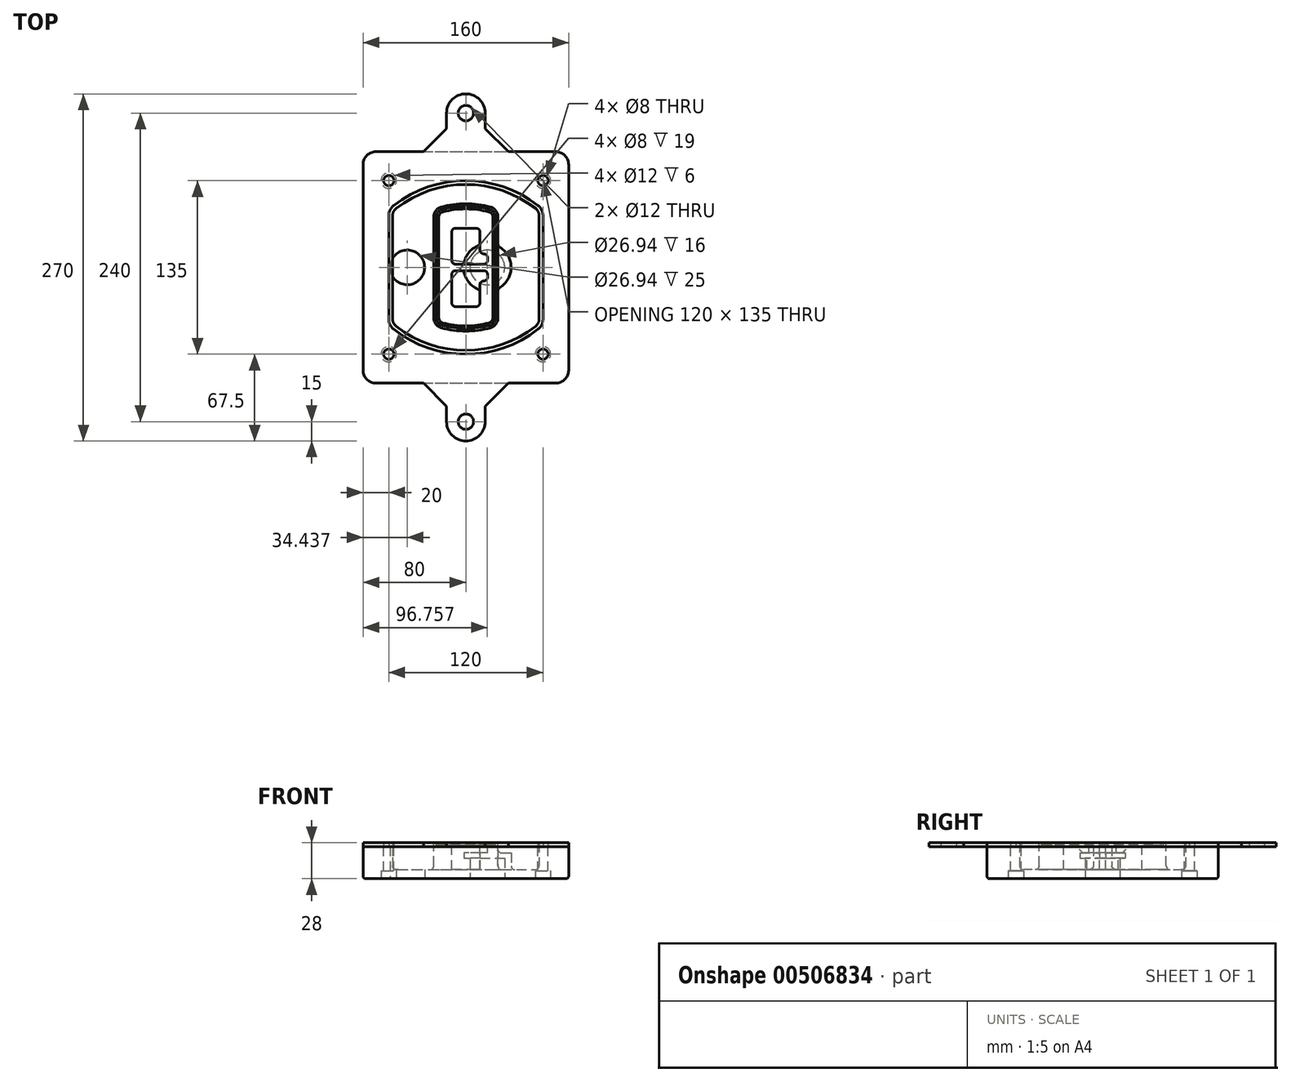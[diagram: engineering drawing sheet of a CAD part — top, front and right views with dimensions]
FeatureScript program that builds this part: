
annotation { "Feature Type Name" : "Feature", "Feature Type Description" : "" }
export const myFeature = defineFeature(function(context is Context, id is Id, definition is map)
    precondition{}
    {
        {
            var Q0;
            Q0=qCreatedBy(makeId("Top.planeOp"),FACE);
            var sketch = newSketch(context, id + "F0", { "sketchPlane" : qUnion([Q0])});
            skPoint(sketch, "E0.rect.middle", {"position": v(0, 0) * mm});
            skLineSegment(sketch, "E1.bottom", {"start": v(-70, -90) * mm, "end": v(70, -90) * mm});
            skLineSegment(sketch, "E1.top", {"start": v(-70, 90) * mm, "end": v(70, 90) * mm});
            skLineSegment(sketch, "E1.left", {"start": v(-80, -80) * mm, "end": v(-80, 80) * mm});
            skLineSegment(sketch, "E1.right", {"start": v(80, -80) * mm, "end": v(80, 80) * mm});
            skLineSegment(sketch, "E2", {"start": v(-80, 90) * mm, "end": v(80, -90) * mm, "construction": true});
            skLineSegment(sketch, "E3", {"start": v(80, 90) * mm, "end": v(-80, -90) * mm, "construction": true});
            skCircle(sketch, "E4", {"center": v(-60, 67.5) * mm, "radius": 4 * mm});
            skCircle(sketch, "E5", {"center": v(60, 67.5) * mm, "radius": 4 * mm});
            skCircle(sketch, "E6", {"center": v(60, -67.5) * mm, "radius": 4 * mm});
            skCircle(sketch, "E7", {"center": v(-60, -67.5) * mm, "radius": 4 * mm});
            skLineSegment(sketch, "E8", {"start": v(-60, 67.5) * mm, "end": v(60, 67.5) * mm, "construction": true});
            skLineSegment(sketch, "E9", {"start": v(60, 67.5) * mm, "end": v(60, -67.5) * mm, "construction": true});
            skLineSegment(sketch, "E10", {"start": v(60, -67.5) * mm, "end": v(-60, -67.5) * mm, "construction": true});
            skLineSegment(sketch, "E11", {"start": v(-60, -67.5) * mm, "end": v(-60, 67.5) * mm, "construction": true});
            skLineSegment(sketch, "E12", {"start": v(-60, 40.3) * mm, "end": v(-60, -40.3) * mm});
            skLineSegment(sketch, "E13", {"start": v(60, 40.3) * mm, "end": v(60, -40.3) * mm});
            skArc(sketch, "E14", {"start": v(56.15, 48.18) * mm, "mid": v(0, 67.5) * mm, "end": v(-56.15, 48.18) * mm});
            skArc(sketch, "E15", {"start": v(-56.15, -48.18) * mm, "mid": v(0, -67.5) * mm, "end": v(56.15, -48.18) * mm});
            skLineSegment(sketch, "E16", {"start": v(-60, 0) * mm, "end": v(60, 0) * mm, "construction": true});
            skPoint(sketch, "E17.visualSharp", {"position": v(-60, -45) * mm});
            skArc(sketch, "E17.filletArc", {"start": v(-60, -40.3) * mm, "mid": v(-58.99, -44.68) * mm, "end": v(-56.15, -48.18) * mm});
            skPoint(sketch, "E18.visualSharp", {"position": v(-60, 45) * mm});
            skArc(sketch, "E18.filletArc", {"start": v(-56.15, 48.18) * mm, "mid": v(-58.99, 44.68) * mm, "end": v(-60, 40.3) * mm});
            skPoint(sketch, "E19.visualSharp", {"position": v(60, 45) * mm});
            skArc(sketch, "E19.filletArc", {"start": v(60, 40.3) * mm, "mid": v(58.99, 44.68) * mm, "end": v(56.15, 48.18) * mm});
            skPoint(sketch, "E20.visualSharp", {"position": v(60, -45) * mm});
            skArc(sketch, "E20.filletArc", {"start": v(56.15, -48.18) * mm, "mid": v(58.99, -44.68) * mm, "end": v(60, -40.3) * mm});
            skPoint(sketch, "E21.visualSharp", {"position": v(-80, 90) * mm});
            skArc(sketch, "E21.filletArc", {"start": v(-70, 90) * mm, "mid": v(-77.07, 87.07) * mm, "end": v(-80, 80) * mm});
            skPoint(sketch, "E22.visualSharp", {"position": v(80, 90) * mm});
            skArc(sketch, "E22.filletArc", {"start": v(80, 80) * mm, "mid": v(77.07, 87.07) * mm, "end": v(70, 90) * mm});
            skPoint(sketch, "E23.visualSharp", {"position": v(80, -90) * mm});
            skArc(sketch, "E23.filletArc", {"start": v(70, -90) * mm, "mid": v(77.07, -87.07) * mm, "end": v(80, -80) * mm});
            skPoint(sketch, "E24.visualSharp", {"position": v(-80, -90) * mm});
            skArc(sketch, "E24.filletArc", {"start": v(-80, -80) * mm, "mid": v(-77.07, -87.07) * mm, "end": v(-70, -90) * mm});
            skArc(sketch, "E25.0", {"start": v(57, 40.3) * mm, "mid": v(56.3, 43.36) * mm, "end": v(54.3, 45.81) * mm});
            skLineSegment(sketch, "E25.1", {"start": v(57, 40.3) * mm, "end": v(57, -40.3) * mm});
            skArc(sketch, "E25.2", {"start": v(54.3, -45.81) * mm, "mid": v(56.3, -43.36) * mm, "end": v(57, -40.3) * mm});
            skArc(sketch, "E25.3", {"start": v(-54.3, -45.81) * mm, "mid": v(0, -64.5) * mm, "end": v(54.3, -45.81) * mm});
            skArc(sketch, "E25.4", {"start": v(-57, -40.3) * mm, "mid": v(-56.3, -43.36) * mm, "end": v(-54.3, -45.81) * mm});
            skArc(sketch, "E25.5", {"start": v(54.3, 45.81) * mm, "mid": v(0, 64.5) * mm, "end": v(-54.3, 45.81) * mm});
            skLineSegment(sketch, "E25.6", {"start": v(-57, 40.3) * mm, "end": v(-57, -40.3) * mm});
            skArc(sketch, "E25.7", {"start": v(-54.3, 45.81) * mm, "mid": v(-56.3, 43.36) * mm, "end": v(-57, 40.3) * mm});
            skArc(sketch, "E26.0", {"start": v(-58.62, 51.33) * mm, "mid": v(-62.58, 46.43) * mm, "end": v(-64, 40.3) * mm});
            skArc(sketch, "E26.1", {"start": v(58.62, 51.33) * mm, "mid": v(0, 71.5) * mm, "end": v(-58.62, 51.33) * mm});
            skArc(sketch, "E26.2", {"start": v(64, 40.3) * mm, "mid": v(62.58, 46.43) * mm, "end": v(58.62, 51.33) * mm});
            skLineSegment(sketch, "E26.3", {"start": v(64, 40.3) * mm, "end": v(64, -40.3) * mm});
            skArc(sketch, "E26.4", {"start": v(58.62, -51.33) * mm, "mid": v(62.58, -46.43) * mm, "end": v(64, -40.3) * mm});
            skLineSegment(sketch, "E26.5", {"start": v(-64, 40.3) * mm, "end": v(-64, -40.3) * mm});
            skArc(sketch, "E26.6", {"start": v(-58.62, -51.33) * mm, "mid": v(0, -71.5) * mm, "end": v(58.62, -51.33) * mm});
            skArc(sketch, "E26.7", {"start": v(-64, -40.3) * mm, "mid": v(-62.58, -46.43) * mm, "end": v(-58.62, -51.33) * mm});
            skSolve(sketch);
        }
        {
            var Q0;
            Q0=makeQuery(id+"F0.imprint","IMPRINT",FACE,{"disambiguationData":[TD([[makeQuery(id+"F0.imprint","IMPRINT",EDGE,{"derivedFrom":sQuery(id+"F0.wireOp",EDGE,"E1.bottom")}),1.0]])]});
            var Q1;
            Q1=makeQuery(id+"F0.imprint","IMPRINT",FACE,{"disambiguationData":[TD([[makeQuery(id+"F0.imprint","IMPRINT",EDGE,{"derivedFrom":sQuery(id+"F0.wireOp",EDGE,"E12")}),1.0]])]});
            var Q2;
            Q2=makeQuery(id+"F0.imprint","IMPRINT",FACE,{"disambiguationData":[TD([[makeQuery(id+"F0.imprint","IMPRINT",EDGE,{"derivedFrom":sQuery(id+"F0.wireOp",EDGE,"E25.0")}),1.0]])]});
            var Q3;
            Q3=makeQuery(id+"F0.imprint","IMPRINT",FACE,{"disambiguationData":[TD([[makeQuery(id+"F0.imprint","IMPRINT",EDGE,{"derivedFrom":sQuery(id+"F0.wireOp",EDGE,"E12")}),-1.0]])]});
            extrude(context, id + "F1", {"entities" : qUnion([Q0, Q1, Q2, Q3]), "oppositeDirection" : true, "depth" : 25 * mm});
        }
        {
            var Q0;
            Q0=makeQuery(id+"F0.imprint","IMPRINT",FACE,{"disambiguationData":[TD([[makeQuery(id+"F0.imprint","IMPRINT",EDGE,{"derivedFrom":sQuery(id+"F0.wireOp",EDGE,"E12")}),1.0]])]});
            extrude(context, id + "F2", {"entities" : qUnion([Q0]), "operationType" : NewBodyOperationType.ADD, "depth" : 3 * mm});
        }
        {
            var Q0;
            Q0=makeQuery(id+"F0.imprint","IMPRINT",FACE,{"disambiguationData":[TD([[makeQuery(id+"F0.imprint","IMPRINT",EDGE,{"derivedFrom":sQuery(id+"F0.wireOp",EDGE,"E25.0")}),1.0]])]});
            extrude(context, id + "F3", {"entities" : qUnion([Q0]), "operationType" : NewBodyOperationType.REMOVE, "oppositeDirection" : true, "depth" : 18 * mm});
        }
        {
            var Q0;
            Q0=makeQuery(id+"F2.opExtrude","CAP_FACE",FACE,{"disambiguationData":[OSD([sQuery(id+"F0.wireOp",EDGE,"E12"),sQuery(id+"F0.wireOp",EDGE,"E13"),sQuery(id+"F0.wireOp",EDGE,"E14"),sQuery(id+"F0.wireOp",EDGE,"E15"),sQuery(id+"F0.wireOp",EDGE,"E17.filletArc"),sQuery(id+"F0.wireOp",EDGE,"E18.filletArc"),sQuery(id+"F0.wireOp",EDGE,"E19.filletArc"),sQuery(id+"F0.wireOp",EDGE,"E20.filletArc"),sQuery(id+"F0.wireOp",EDGE,"E25.0"),sQuery(id+"F0.wireOp",EDGE,"E25.1"),sQuery(id+"F0.wireOp",EDGE,"E25.2"),sQuery(id+"F0.wireOp",EDGE,"E25.3"),sQuery(id+"F0.wireOp",EDGE,"E25.4"),sQuery(id+"F0.wireOp",EDGE,"E25.5"),sQuery(id+"F0.wireOp",EDGE,"E25.6"),sQuery(id+"F0.wireOp",EDGE,"E25.7")])],"isStart":false});
            var sketch = newSketch(context, id + "F4", { "sketchPlane" : qUnion([Q0])});
            skArc(sketch, "E27.0", {"start": v(-19.08, -46.97) * mm, "mid": v(0, -49.5) * mm, "end": v(19.08, -46.97) * mm});
            skArc(sketch, "E28.0", {"start": v(19.08, 46.97) * mm, "mid": v(0, 49.5) * mm, "end": v(-19.08, 46.97) * mm});
            skLineSegment(sketch, "E29", {"start": v(-25, 39.25) * mm, "end": v(-25, -39.25) * mm});
            skLineSegment(sketch, "E30", {"start": v(25, 39.25) * mm, "end": v(25, -39.25) * mm});
            skLineSegment(sketch, "E31", {"start": v(-25, 45.1) * mm, "end": v(25, 45.1) * mm, "construction": true});
            skLineSegment(sketch, "E32", {"start": v(-25, -45.1) * mm, "end": v(25, -45.1) * mm, "construction": true});
            skPoint(sketch, "E33.visualSharp", {"position": v(-25, 45.1) * mm});
            skArc(sketch, "E33.filletArc", {"start": v(-19.08, 46.97) * mm, "mid": v(-23.35, 44.11) * mm, "end": v(-25, 39.25) * mm});
            skPoint(sketch, "E34.visualSharp", {"position": v(25, 45.1) * mm});
            skArc(sketch, "E34.filletArc", {"start": v(25, 39.25) * mm, "mid": v(23.35, 44.11) * mm, "end": v(19.08, 46.97) * mm});
            skPoint(sketch, "E35.visualSharp", {"position": v(25, -45.1) * mm});
            skArc(sketch, "E35.filletArc", {"start": v(19.08, -46.97) * mm, "mid": v(23.35, -44.11) * mm, "end": v(25, -39.25) * mm});
            skPoint(sketch, "E36.visualSharp", {"position": v(-25, -45.1) * mm});
            skArc(sketch, "E36.filletArc", {"start": v(-25, -39.25) * mm, "mid": v(-23.35, -44.11) * mm, "end": v(-19.08, -46.97) * mm});
            skArc(sketch, "E37.0", {"start": v(54.3, 45.81) * mm, "mid": v(0, 64.5) * mm, "end": v(-54.3, 45.81) * mm});
            skArc(sketch, "E37.1", {"start": v(-54.3, 45.81) * mm, "mid": v(-56.3, 43.36) * mm, "end": v(-57, 40.3) * mm});
            skLineSegment(sketch, "E37.2", {"start": v(-57, 40.3) * mm, "end": v(-57, -40.3) * mm});
            skArc(sketch, "E37.3", {"start": v(-57, -40.3) * mm, "mid": v(-56.3, -43.36) * mm, "end": v(-54.3, -45.81) * mm});
            skArc(sketch, "E37.4", {"start": v(-54.3, -45.81) * mm, "mid": v(0, -64.5) * mm, "end": v(54.3, -45.81) * mm});
            skArc(sketch, "E37.5", {"start": v(54.3, -45.81) * mm, "mid": v(56.3, -43.36) * mm, "end": v(57, -40.3) * mm});
            skLineSegment(sketch, "E37.6", {"start": v(57, 40.3) * mm, "end": v(57, -40.3) * mm});
            skArc(sketch, "E37.7", {"start": v(57, 40.3) * mm, "mid": v(56.3, 43.36) * mm, "end": v(54.3, 45.81) * mm});
            skLineSegment(sketch, "E38.0", {"start": v(23, 39.25) * mm, "end": v(23, -39.25) * mm});
            skArc(sketch, "E38.1", {"start": v(18.56, -45.04) * mm, "mid": v(21.76, -42.9) * mm, "end": v(23, -39.25) * mm});
            skArc(sketch, "E38.2", {"start": v(-18.56, -45.04) * mm, "mid": v(0, -47.5) * mm, "end": v(18.56, -45.04) * mm});
            skArc(sketch, "E38.3", {"start": v(-23, -39.25) * mm, "mid": v(-21.76, -42.9) * mm, "end": v(-18.56, -45.04) * mm});
            skLineSegment(sketch, "E38.4", {"start": v(-23, 39.25) * mm, "end": v(-23, -39.25) * mm});
            skArc(sketch, "E38.5", {"start": v(23, 39.25) * mm, "mid": v(21.76, 42.9) * mm, "end": v(18.56, 45.04) * mm});
            skArc(sketch, "E38.6", {"start": v(-18.56, 45.04) * mm, "mid": v(-21.76, 42.9) * mm, "end": v(-23, 39.25) * mm});
            skArc(sketch, "E38.7", {"start": v(18.56, 45.04) * mm, "mid": v(0, 47.5) * mm, "end": v(-18.56, 45.04) * mm});
            skArc(sketch, "E39.0", {"start": v(21, 39.25) * mm, "mid": v(20.18, 41.68) * mm, "end": v(18.04, 43.1) * mm});
            skLineSegment(sketch, "E39.1", {"start": v(21, 39.25) * mm, "end": v(21, -39.25) * mm});
            skArc(sketch, "E39.2", {"start": v(18.04, -43.1) * mm, "mid": v(20.18, -41.68) * mm, "end": v(21, -39.25) * mm});
            skArc(sketch, "E39.3", {"start": v(-18.04, -43.1) * mm, "mid": v(0, -45.5) * mm, "end": v(18.04, -43.1) * mm});
            skArc(sketch, "E39.4", {"start": v(-21, -39.25) * mm, "mid": v(-20.18, -41.68) * mm, "end": v(-18.04, -43.1) * mm});
            skArc(sketch, "E39.5", {"start": v(18.04, 43.1) * mm, "mid": v(0, 45.5) * mm, "end": v(-18.04, 43.1) * mm});
            skLineSegment(sketch, "E39.6", {"start": v(-21, 39.25) * mm, "end": v(-21, -39.25) * mm});
            skArc(sketch, "E39.7", {"start": v(-18.04, 43.1) * mm, "mid": v(-20.18, 41.68) * mm, "end": v(-21, 39.25) * mm});
            skLineSegment(sketch, "E40", {"start": v(-25, 0) * mm, "end": v(25, 0) * mm, "construction": true});
            skLineSegment(sketch, "E41", {"start": v(-11, 5.5) * mm, "end": v(-11, 27.5) * mm});
            skLineSegment(sketch, "E42", {"start": v(-8, 30.5) * mm, "end": v(8, 30.5) * mm});
            skLineSegment(sketch, "E43", {"start": v(11, 27.5) * mm, "end": v(11, 13.5) * mm});
            skLineSegment(sketch, "E44", {"start": v(14, 10.5) * mm, "end": v(14, 10.5) * mm});
            skLineSegment(sketch, "E45", {"start": v(17, 7.5) * mm, "end": v(17, 5.5) * mm});
            skLineSegment(sketch, "E46", {"start": v(14, 2.5) * mm, "end": v(-8, 2.5) * mm});
            skPoint(sketch, "E47.visualSharp", {"position": v(-11, 30.5) * mm});
            skArc(sketch, "E47.filletArc", {"start": v(-8, 30.5) * mm, "mid": v(-10.12, 29.62) * mm, "end": v(-11, 27.5) * mm});
            skPoint(sketch, "E48.visualSharp", {"position": v(11, 30.5) * mm});
            skArc(sketch, "E48.filletArc", {"start": v(11, 27.5) * mm, "mid": v(10.12, 29.62) * mm, "end": v(8, 30.5) * mm});
            skPoint(sketch, "E49.visualSharp", {"position": v(11, 10.5) * mm});
            skArc(sketch, "E49.filletArc", {"start": v(11, 13.5) * mm, "mid": v(11.88, 11.38) * mm, "end": v(14, 10.5) * mm});
            skPoint(sketch, "E50.visualSharp", {"position": v(17, 10.5) * mm});
            skArc(sketch, "E50.filletArc", {"start": v(17, 7.5) * mm, "mid": v(16.12, 9.62) * mm, "end": v(14, 10.5) * mm});
            skPoint(sketch, "E51.visualSharp", {"position": v(17, 2.5) * mm});
            skArc(sketch, "E51.filletArc", {"start": v(14, 2.5) * mm, "mid": v(16.12, 3.38) * mm, "end": v(17, 5.5) * mm});
            skPoint(sketch, "E52.visualSharp", {"position": v(-11, 2.5) * mm});
            skArc(sketch, "E52.filletArc", {"start": v(-11, 5.5) * mm, "mid": v(-10.12, 3.38) * mm, "end": v(-8, 2.5) * mm});
            skLineSegment(sketch, "E53.0.MirrorCS", {"start": v(14, -2.5) * mm, "end": v(-8, -2.5) * mm});
            skArc(sketch, "E54.0.MirrorCS", {"start": v(-11, -5.5) * mm, "mid": v(-10.12, -3.38) * mm, "end": v(-8, -2.5) * mm});
            skLineSegment(sketch, "E55.0.MirrorCS", {"start": v(-11, -5.5) * mm, "end": v(-11, -27.5) * mm});
            skArc(sketch, "E56.0.MirrorCS", {"start": v(-8, -30.5) * mm, "mid": v(-10.12, -29.62) * mm, "end": v(-11, -27.5) * mm});
            skLineSegment(sketch, "E57.0.MirrorCS", {"start": v(-8, -30.5) * mm, "end": v(8, -30.5) * mm});
            skArc(sketch, "E58.0.MirrorCS", {"start": v(11, -27.5) * mm, "mid": v(10.12, -29.62) * mm, "end": v(8, -30.5) * mm});
            skLineSegment(sketch, "E59.0.MirrorCS", {"start": v(11, -27.5) * mm, "end": v(11, -13.5) * mm});
            skArc(sketch, "E60.0.MirrorCS", {"start": v(11, -13.5) * mm, "mid": v(11.88, -11.38) * mm, "end": v(14, -10.5) * mm});
            skArc(sketch, "E61.0.MirrorCS", {"start": v(17, -7.5) * mm, "mid": v(16.12, -9.62) * mm, "end": v(14, -10.5) * mm});
            skLineSegment(sketch, "E62.0.MirrorCS", {"start": v(17, -7.5) * mm, "end": v(17, -5.5) * mm});
            skArc(sketch, "E63.0.MirrorCS", {"start": v(14, -2.5) * mm, "mid": v(16.12, -3.38) * mm, "end": v(17, -5.5) * mm});
            skSolve(sketch);
        }
        {
            var Q0;
            Q0=makeQuery(id+"F4.imprint","IMPRINT",FACE,{"disambiguationData":[TD([[makeQuery(id+"F4.imprint","IMPRINT",EDGE,{"derivedFrom":sQuery(id+"F4.wireOp",EDGE,"E27.0")}),1.0]])]});
            var Q1;
            Q1=makeQuery(id+"F4.imprint","IMPRINT",FACE,{"disambiguationData":[TD([[makeQuery(id+"F4.imprint","IMPRINT",EDGE,{"derivedFrom":sQuery(id+"F4.wireOp",EDGE,"E38.0")}),-1.0]])]});
            var Q2;
            Q2=makeQuery(id+"F4.imprint","IMPRINT",FACE,{"disambiguationData":[TD([[makeQuery(id+"F4.imprint","IMPRINT",EDGE,{"derivedFrom":sQuery(id+"F4.wireOp",EDGE,"E39.0")}),1.0]])]});
            extrude(context, id + "F5", {"entities" : qUnion([Q0, Q1, Q2]), "operationType" : NewBodyOperationType.ADD, "endBound" : BoundingType.UP_TO_NEXT, "oppositeDirection" : true, "depth" : 25 * mm});
        }
        {
            var Q0;
            Q0=makeQuery(id+"F4.imprint","IMPRINT",FACE,{"disambiguationData":[TD([[makeQuery(id+"F4.imprint","IMPRINT",EDGE,{"derivedFrom":sQuery(id+"F4.wireOp",EDGE,"E38.0")}),-1.0]])]});
            extrude(context, id + "F6", {"entities" : qUnion([Q0]), "operationType" : NewBodyOperationType.REMOVE, "oppositeDirection" : true, "depth" : 2 * mm});
        }
        {
            var Q0;
            Q0=makeQuery(id+"F1.opExtrude","CAP_FACE",FACE,{"disambiguationData":[OSD([sQuery(id+"F0.wireOp",EDGE,"E1.bottom"),sQuery(id+"F0.wireOp",EDGE,"E1.top"),sQuery(id+"F0.wireOp",EDGE,"E1.left"),sQuery(id+"F0.wireOp",EDGE,"E1.right"),sQuery(id+"F0.wireOp",EDGE,"E4"),sQuery(id+"F0.wireOp",EDGE,"E5"),sQuery(id+"F0.wireOp",EDGE,"E6"),sQuery(id+"F0.wireOp",EDGE,"E7"),sQuery(id+"F0.wireOp",EDGE,"E21.filletArc"),sQuery(id+"F0.wireOp",EDGE,"E22.filletArc"),sQuery(id+"F0.wireOp",EDGE,"E23.filletArc"),sQuery(id+"F0.wireOp",EDGE,"E24.filletArc")])],"isStart":false});
            var sketch = newSketch(context, id + "F7", { "sketchPlane" : qUnion([Q0])});
            skCircle(sketch, "E64", {"center": v(16.76, 0) * mm, "radius": 13.47 * mm});
            skCircle(sketch, "E65", {"center": v(-45.56, 0) * mm, "radius": 13.47 * mm});
            skLineSegment(sketch, "E66", {"start": v(80, 0) * mm, "end": v(-80, 0) * mm});
            skCircle(sketch, "E67", {"center": v(16.76, 0) * mm, "radius": 18.47 * mm});
            skCircle(sketch, "E68", {"center": v(60, -67.5) * mm, "radius": 6 * mm});
            skCircle(sketch, "E69", {"center": v(-60, -67.5) * mm, "radius": 6 * mm});
            skCircle(sketch, "E70", {"center": v(-60, 67.5) * mm, "radius": 6 * mm});
            skCircle(sketch, "E71", {"center": v(60, 67.5) * mm, "radius": 6 * mm});
            skSolve(sketch);
        }
        {
            var Q0;
            {var subQ1=sQuery(id+"F7.wireOp",EDGE,"E66");var subQ4=sQuery(id+"F7.wireOp",EDGE,"E64");var subQ6=makeQuery(id+"F7.imprint","INTERSECT",VERTEX,{"disambiguationData":[OD(0.0)],"derivedFrom":[subQ4,subQ1]});Q0=makeQuery(id+"F7.imprint","IMPRINT",FACE,{"disambiguationData":[TD([[makeQuery(id+"F7.imprint","IMPRINT",EDGE,{"disambiguationData":[TD([[subQ6,-1.0]])],"derivedFrom":subQ4}),-1.0]])]});}
            var Q1;
            {var subQ0=sQuery(id+"F7.wireOp",EDGE,"E66");var subQ1=sQuery(id+"F7.wireOp",EDGE,"E64");var subQ3=makeQuery(id+"F7.imprint","INTERSECT",VERTEX,{"disambiguationData":[OD(0.0)],"derivedFrom":[subQ1,subQ0]});Q1=makeQuery(id+"F7.imprint","IMPRINT",FACE,{"disambiguationData":[TD([[makeQuery(id+"F7.imprint","IMPRINT",EDGE,{"disambiguationData":[TD([[subQ3,-1.0]])],"derivedFrom":subQ1}),1.0]])]});}
            var Q2;
            {var subQ0=sQuery(id+"F7.wireOp",EDGE,"E66");var subQ1=sQuery(id+"F7.wireOp",EDGE,"E64");var subQ3=makeQuery(id+"F7.imprint","INTERSECT",VERTEX,{"disambiguationData":[OD(0.0)],"derivedFrom":[subQ1,subQ0]});Q2=makeQuery(id+"F7.imprint","IMPRINT",FACE,{"disambiguationData":[TD([[makeQuery(id+"F7.imprint","IMPRINT",EDGE,{"disambiguationData":[TD([[subQ3,1.0]])],"derivedFrom":subQ1}),1.0]])]});}
            var Q3;
            {var subQ1=sQuery(id+"F7.wireOp",EDGE,"E66");var subQ4=sQuery(id+"F7.wireOp",EDGE,"E64");var subQ6=makeQuery(id+"F7.imprint","INTERSECT",VERTEX,{"disambiguationData":[OD(0.0)],"derivedFrom":[subQ4,subQ1]});Q3=makeQuery(id+"F7.imprint","IMPRINT",FACE,{"disambiguationData":[TD([[makeQuery(id+"F7.imprint","IMPRINT",EDGE,{"disambiguationData":[TD([[subQ6,1.0]])],"derivedFrom":subQ4}),-1.0]])]});}
            extrude(context, id + "F8", {"entities" : qUnion([Q0, Q1, Q2, Q3]), "operationType" : NewBodyOperationType.ADD, "oppositeDirection" : true, "depth" : 20 * mm});
        }
        {
            var Q0;
            {var subQ0=sQuery(id+"F7.wireOp",EDGE,"E66");var subQ1=sQuery(id+"F7.wireOp",EDGE,"E64");var subQ3=makeQuery(id+"F7.imprint","INTERSECT",VERTEX,{"disambiguationData":[OD(0.0)],"derivedFrom":[subQ1,subQ0]});Q0=makeQuery(id+"F7.imprint","IMPRINT",FACE,{"disambiguationData":[TD([[makeQuery(id+"F7.imprint","IMPRINT",EDGE,{"disambiguationData":[TD([[subQ3,-1.0]])],"derivedFrom":subQ1}),1.0]])]});}
            var Q1;
            {var subQ0=sQuery(id+"F7.wireOp",EDGE,"E66");var subQ1=sQuery(id+"F7.wireOp",EDGE,"E64");var subQ3=makeQuery(id+"F7.imprint","INTERSECT",VERTEX,{"disambiguationData":[OD(0.0)],"derivedFrom":[subQ1,subQ0]});Q1=makeQuery(id+"F7.imprint","IMPRINT",FACE,{"disambiguationData":[TD([[makeQuery(id+"F7.imprint","IMPRINT",EDGE,{"disambiguationData":[TD([[subQ3,1.0]])],"derivedFrom":subQ1}),1.0]])]});}
            extrude(context, id + "F9", {"entities" : qUnion([Q0, Q1]), "operationType" : NewBodyOperationType.REMOVE, "oppositeDirection" : true, "depth" : 16 * mm});
        }
        {
            var Q0;
            {var subQ0=sQuery(id+"F7.wireOp",EDGE,"E66");var subQ1=sQuery(id+"F7.wireOp",EDGE,"E65");var subQ3=makeQuery(id+"F7.imprint","INTERSECT",VERTEX,{"disambiguationData":[OD(0.0)],"derivedFrom":[subQ1,subQ0]});Q0=makeQuery(id+"F7.imprint","IMPRINT",FACE,{"disambiguationData":[TD([[makeQuery(id+"F7.imprint","IMPRINT",EDGE,{"disambiguationData":[TD([[subQ3,-1.0]])],"derivedFrom":subQ1}),1.0]])]});}
            var Q1;
            {var subQ0=sQuery(id+"F7.wireOp",EDGE,"E66");var subQ1=sQuery(id+"F7.wireOp",EDGE,"E65");var subQ3=makeQuery(id+"F7.imprint","INTERSECT",VERTEX,{"disambiguationData":[OD(0.0)],"derivedFrom":[subQ1,subQ0]});Q1=makeQuery(id+"F7.imprint","IMPRINT",FACE,{"disambiguationData":[TD([[makeQuery(id+"F7.imprint","IMPRINT",EDGE,{"disambiguationData":[TD([[subQ3,1.0]])],"derivedFrom":subQ1}),1.0]])]});}
            extrude(context, id + "F10", {"entities" : qUnion([Q0, Q1]), "operationType" : NewBodyOperationType.REMOVE, "oppositeDirection" : true, "depth" : 25 * mm});
        }
        {
            var Q0;
            Q0=makeQuery(id+"F7.imprint","IMPRINT",FACE,{"disambiguationData":[TD([[makeQuery(id+"F7.imprint","IMPRINT",EDGE,{"derivedFrom":sQuery(id+"F7.wireOp",EDGE,"E68")}),1.0]])]});
            var Q1;
            Q1=makeQuery(id+"F7.imprint","IMPRINT",FACE,{"disambiguationData":[TD([[makeQuery(id+"F7.imprint","IMPRINT",EDGE,{"derivedFrom":makeQuery(id+"F1.opExtrude","CAP_EDGE",EDGE,{"disambiguationData":[OSD([sQuery(id+"F0.wireOp",EDGE,"E5")])],"isStart":false})}),-1.0]])]});
            var Q2;
            Q2=makeQuery(id+"F7.imprint","IMPRINT",FACE,{"disambiguationData":[TD([[makeQuery(id+"F7.imprint","IMPRINT",EDGE,{"derivedFrom":sQuery(id+"F7.wireOp",EDGE,"E69")}),1.0]])]});
            var Q3;
            Q3=makeQuery(id+"F7.imprint","IMPRINT",FACE,{"disambiguationData":[TD([[makeQuery(id+"F7.imprint","IMPRINT",EDGE,{"derivedFrom":makeQuery(id+"F1.opExtrude","CAP_EDGE",EDGE,{"disambiguationData":[OSD([sQuery(id+"F0.wireOp",EDGE,"E4")])],"isStart":false})}),-1.0]])]});
            var Q4;
            Q4=makeQuery(id+"F7.imprint","IMPRINT",FACE,{"disambiguationData":[TD([[makeQuery(id+"F7.imprint","IMPRINT",EDGE,{"derivedFrom":sQuery(id+"F7.wireOp",EDGE,"E70")}),1.0]])]});
            var Q5;
            Q5=makeQuery(id+"F7.imprint","IMPRINT",FACE,{"disambiguationData":[TD([[makeQuery(id+"F7.imprint","IMPRINT",EDGE,{"derivedFrom":makeQuery(id+"F1.opExtrude","CAP_EDGE",EDGE,{"disambiguationData":[OSD([sQuery(id+"F0.wireOp",EDGE,"E7")])],"isStart":false})}),-1.0]])]});
            var Q6;
            Q6=makeQuery(id+"F7.imprint","IMPRINT",FACE,{"disambiguationData":[TD([[makeQuery(id+"F7.imprint","IMPRINT",EDGE,{"derivedFrom":sQuery(id+"F7.wireOp",EDGE,"E71")}),1.0]])]});
            var Q7;
            Q7=makeQuery(id+"F7.imprint","IMPRINT",FACE,{"disambiguationData":[TD([[makeQuery(id+"F7.imprint","IMPRINT",EDGE,{"derivedFrom":makeQuery(id+"F1.opExtrude","CAP_EDGE",EDGE,{"disambiguationData":[OSD([sQuery(id+"F0.wireOp",EDGE,"E6")])],"isStart":false})}),-1.0]])]});
            extrude(context, id + "F11", {"entities" : qUnion([Q0, Q1, Q2, Q3, Q4, Q5, Q6, Q7]), "operationType" : NewBodyOperationType.REMOVE, "oppositeDirection" : true, "depth" : 6 * mm});
        }
        {
            var Q0;
            Q0=makeQuery(id+"F9.boolean.opBoolean","COPY",FACE,{"derivedFrom":makeQuery(id+"F9.opExtrude","CAP_FACE",FACE,{"disambiguationData":[OSD([sQuery(id+"F7.wireOp",EDGE,"E64")])],"isStart":false})});
            var sketch = newSketch(context, id + "F12", { "sketchPlane" : qUnion([Q0])});
            skArc(sketch, "E72.0", {"start": v(11, 17.55) * mm, "mid": v(2.57, 11.82) * mm, "end": v(-1.54, 2.5) * mm});
            skArc(sketch, "E72.1", {"start": v(-1.54, -2.5) * mm, "mid": v(2.57, -11.82) * mm, "end": v(11, -17.55) * mm});
            skLineSegment(sketch, "E73", {"start": v(-1.54, -2.5) * mm, "end": v(14, -2.5) * mm});
            skLineSegment(sketch, "E74.0", {"start": v(14, 2.5) * mm, "end": v(-1.54, 2.5) * mm});
            skArc(sketch, "E74.1", {"start": v(14, 2.5) * mm, "mid": v(16.12, 3.38) * mm, "end": v(17, 5.5) * mm});
            skLineSegment(sketch, "E74.2", {"start": v(17, 7.5) * mm, "end": v(17, 5.5) * mm});
            skArc(sketch, "E74.3", {"start": v(17, 7.5) * mm, "mid": v(16.12, 9.62) * mm, "end": v(14, 10.5) * mm});
            skArc(sketch, "E74.4", {"start": v(11, 13.5) * mm, "mid": v(11.88, 11.38) * mm, "end": v(14, 10.5) * mm});
            skLineSegment(sketch, "E74.5", {"start": v(11, 17.55) * mm, "end": v(11, 13.5) * mm});
            skLineSegment(sketch, "E74.7", {"start": v(14, -2.5) * mm, "end": v(-1.54, -2.5) * mm});
            skArc(sketch, "E74.8", {"start": v(14, -2.5) * mm, "mid": v(16.12, -3.38) * mm, "end": v(17, -5.5) * mm});
            skLineSegment(sketch, "E74.9", {"start": v(17, -7.5) * mm, "end": v(17, -5.5) * mm});
            skArc(sketch, "E74.10", {"start": v(17, -7.5) * mm, "mid": v(16.12, -9.62) * mm, "end": v(14, -10.5) * mm});
            skArc(sketch, "E74.11", {"start": v(11, -13.5) * mm, "mid": v(11.88, -11.38) * mm, "end": v(14, -10.5) * mm});
            skLineSegment(sketch, "E74.12", {"start": v(11, -17.55) * mm, "end": v(11, -13.5) * mm});
            skPoint(sketch, "E75.orphan", {"position": v(11, -27.5) * mm});
            skPoint(sketch, "E76.orphan", {"position": v(-8, -2.5) * mm});
            skPoint(sketch, "E77.orphan", {"position": v(-8, 2.5) * mm});
            skPoint(sketch, "E78.orphan", {"position": v(11, 27.5) * mm});
            skSolve(sketch);
        }
        {
            var Q0;
            {var subQ7=sQuery(id+"F12.wireOp",EDGE,"E72.0");var subQ14=sQuery(id+"F12.wireOp",EDGE,"E72.1");var subQ16=sQuery(id+"F12.wireOp",EDGE,"E74.1");var subQ18=sQuery(id+"F12.wireOp",EDGE,"E74.8");Q0=qUnion([makeQuery(id+"F12.imprint","IMPRINT",FACE,{"disambiguationData":[TD([[makeQuery(id+"F12.imprint","IMPRINT",EDGE,{"derivedFrom":subQ7}),1.0]])]}),makeQuery(id+"F12.imprint","IMPRINT",FACE,{"disambiguationData":[TD([[makeQuery(id+"F12.imprint","IMPRINT",EDGE,{"derivedFrom":subQ14}),1.0]])]}),makeQuery(id+"F12.imprint","IMPRINT",FACE,{"disambiguationData":[TD([[makeQuery(id+"F12.imprint","IMPRINT",EDGE,{"derivedFrom":subQ16}),1.0]])]}),makeQuery(id+"F12.imprint","IMPRINT",FACE,{"disambiguationData":[TD([[makeQuery(id+"F12.imprint","IMPRINT",EDGE,{"derivedFrom":subQ18}),-1.0]])]})]);}
            var Q1;
            Q1=makeQuery(id+"F5.boolean.opBoolean","SPLIT",FACE,{"disambiguationData":[TD([makeQuery(id+"F5.opExtrude","SWEPT_FACE",FACE,{"disambiguationData":[OSD([sQuery(id+"F4.wireOp",EDGE,"E41")])]})])],"derivedFrom":makeQuery(id+"F3.boolean.opBoolean","COPY",FACE,{"derivedFrom":makeQuery(id+"F3.opExtrude","CAP_FACE",FACE,{"disambiguationData":[OSD([sQuery(id+"F0.wireOp",EDGE,"E25.0"),sQuery(id+"F0.wireOp",EDGE,"E25.1"),sQuery(id+"F0.wireOp",EDGE,"E25.2"),sQuery(id+"F0.wireOp",EDGE,"E25.3"),sQuery(id+"F0.wireOp",EDGE,"E25.4"),sQuery(id+"F0.wireOp",EDGE,"E25.5"),sQuery(id+"F0.wireOp",EDGE,"E25.6"),sQuery(id+"F0.wireOp",EDGE,"E25.7")])],"isStart":false})})});
            extrude(context, id + "F13", {"entities" : qUnion([Q0]), "operationType" : NewBodyOperationType.REMOVE, "endBound" : BoundingType.UP_TO_SURFACE, "endBoundEntityFace" : qUnion([Q1]), "depth" : 25 * mm});
        }
        {
            var Q0;
            Q0=makeQuery(id+"F3.boolean.opBoolean","COPY",EDGE,{"derivedFrom":makeQuery(id+"F3.opExtrude","CAP_EDGE",EDGE,{"disambiguationData":[OSD([sQuery(id+"F0.wireOp",EDGE,"E25.6")])],"isStart":false})});
            var Q1;
            Q1=makeQuery(id+"F8.boolean.opBoolean","INTERSECT",EDGE,{"derivedFrom":[makeQuery(id+"F5.opExtrude","SWEPT_FACE",FACE,{"disambiguationData":[OSD([sQuery(id+"F4.wireOp",EDGE,"E30")])]}),makeQuery(id+"F8.opExtrude","CAP_FACE",FACE,{"disambiguationData":[OSD([sQuery(id+"F7.wireOp",EDGE,"E67")])],"isStart":false})]});
            var Q2;
            Q2=makeQuery(id+"F8.boolean.opBoolean","INTERSECT",EDGE,{"disambiguationData":[OD(1.0)],"derivedFrom":[makeQuery(id+"F5.opExtrude","SWEPT_FACE",FACE,{"disambiguationData":[OSD([sQuery(id+"F4.wireOp",EDGE,"E30")])]}),makeQuery(id+"F8.opExtrude","SWEPT_FACE",FACE,{"disambiguationData":[OSD([sQuery(id+"F7.wireOp",EDGE,"E67")])]})]});
            var Q3;
            {var subQ0=sQuery(id+"F4.wireOp",EDGE,"E30");Q3=makeQuery(id+"F8.boolean.opBoolean","SPLIT",EDGE,{"disambiguationData":[TD([makeQuery(id+"F5.opExtrude","SWEPT_FACE",FACE,{"disambiguationData":[OSD([sQuery(id+"F4.wireOp",EDGE,"E35.filletArc")])]})])],"derivedFrom":makeQuery(id+"F5.opExtrude","CAP_EDGE",EDGE,{"disambiguationData":[OSD([subQ0])],"isStart":false})});}
            var Q4;
            {var subQ0=sQuery(id+"F0.wireOp",EDGE,"E25.7");var subQ1=sQuery(id+"F0.wireOp",EDGE,"E25.1");var subQ2=sQuery(id+"F0.wireOp",EDGE,"E25.6");var subQ3=sQuery(id+"F0.wireOp",EDGE,"E25.5");var subQ4=sQuery(id+"F0.wireOp",EDGE,"E25.4");var subQ5=sQuery(id+"F0.wireOp",EDGE,"E25.0");var subQ6=sQuery(id+"F0.wireOp",EDGE,"E25.2");var subQ7=sQuery(id+"F0.wireOp",EDGE,"E25.3");Q4=makeQuery(id+"F8.boolean.opBoolean","INTERSECT",EDGE,{"derivedFrom":[makeQuery(id+"F5.boolean.opBoolean","SPLIT",FACE,{"disambiguationData":[TD([makeQuery(id+"F2.opExtrude","SWEPT_FACE",FACE,{"disambiguationData":[OSD([subQ5])]})])],"derivedFrom":makeQuery(id+"F3.boolean.opBoolean","COPY",FACE,{"derivedFrom":makeQuery(id+"F3.opExtrude","CAP_FACE",FACE,{"disambiguationData":[OSD([subQ5,subQ1,subQ6,subQ7,subQ4,subQ3,subQ2,subQ0])],"isStart":false})})}),makeQuery(id+"F8.opExtrude","SWEPT_FACE",FACE,{"disambiguationData":[OSD([sQuery(id+"F7.wireOp",EDGE,"E67")])]})]});}
            var Q5;
            Q5=makeQuery(id+"F8.boolean.opBoolean","INTERSECT",EDGE,{"disambiguationData":[OD(0.0)],"derivedFrom":[makeQuery(id+"F5.opExtrude","SWEPT_FACE",FACE,{"disambiguationData":[OSD([sQuery(id+"F4.wireOp",EDGE,"E30")])]}),makeQuery(id+"F8.opExtrude","SWEPT_FACE",FACE,{"disambiguationData":[OSD([sQuery(id+"F7.wireOp",EDGE,"E67")])]})]});
            fillet(context, id + "F14", {"entities" : qUnion([Q0, Q1, Q2, Q3, Q4, Q5]), "radius" : 3 * mm, "tangentPropagation" : true, "allowEdgeOverflow" : false});
        }
        {
            var Q0;
            Q0=makeQuery(id+"F1.opExtrude","CAP_EDGE",EDGE,{"disambiguationData":[OSD([sQuery(id+"F0.wireOp",EDGE,"E1.bottom")])],"isStart":false});
            fillet(context, id + "F15", {"entities" : qUnion([Q0]), "radius" : 2 * mm, "tangentPropagation" : true, "allowEdgeOverflow" : false});
        }
        {
            var Q0;
            {var subQ0=sQuery(id+"F0.wireOp",EDGE,"E21.filletArc");var subQ1=sQuery(id+"F0.wireOp",EDGE,"E7");var subQ2=sQuery(id+"F0.wireOp",EDGE,"E6");var subQ3=sQuery(id+"F0.wireOp",EDGE,"E5");var subQ4=sQuery(id+"F0.wireOp",EDGE,"E4");var subQ5=sQuery(id+"F0.wireOp",EDGE,"E22.filletArc");var subQ6=sQuery(id+"F0.wireOp",EDGE,"E1.bottom");var subQ7=sQuery(id+"F0.wireOp",EDGE,"E1.right");var subQ8=sQuery(id+"F0.wireOp",EDGE,"E1.top");var subQ9=sQuery(id+"F0.wireOp",EDGE,"E1.left");var subQ10=sQuery(id+"F0.wireOp",EDGE,"E23.filletArc");var subQ11=sQuery(id+"F0.wireOp",EDGE,"E24.filletArc");Q0=makeQuery(id+"F2.boolean.opBoolean","SPLIT",FACE,{"disambiguationData":[TD([makeQuery(id+"F1.opExtrude","SWEPT_FACE",FACE,{"disambiguationData":[OSD([subQ6])]})])],"derivedFrom":makeQuery(id+"F1.opExtrude","CAP_FACE",FACE,{"disambiguationData":[OSD([subQ6,subQ8,subQ9,subQ7,subQ4,subQ3,subQ2,subQ1,subQ0,subQ5,subQ10,subQ11])],"isStart":true})});}
            var sketch = newSketch(context, id + "F16", { "sketchPlane" : qUnion([Q0])});
            skLineSegment(sketch, "E79.0", {"start": v(70, 90) * mm, "end": v(-70, 90) * mm});
            skArc(sketch, "E79.1", {"start": v(-70, 90) * mm, "mid": v(-77.07, 87.07) * mm, "end": v(-80, 80) * mm});
            skLineSegment(sketch, "E79.2", {"start": v(-80, -80) * mm, "end": v(-80, 80) * mm});
            skCircle(sketch, "E79.3", {"center": v(-60, 67.5) * mm, "radius": 4 * mm});
            skArc(sketch, "E79.4", {"start": v(56.15, 48.18) * mm, "mid": v(0, 67.5) * mm, "end": v(-56.15, 48.18) * mm});
            skArc(sketch, "E79.5", {"start": v(-56.15, 48.18) * mm, "mid": v(-58.99, 44.68) * mm, "end": v(-60, 40.3) * mm});
            skLineSegment(sketch, "E79.6", {"start": v(-60, 40.3) * mm, "end": v(-60, -40.3) * mm});
            skArc(sketch, "E79.7", {"start": v(-60, -40.3) * mm, "mid": v(-58.99, -44.68) * mm, "end": v(-56.15, -48.18) * mm});
            skArc(sketch, "E79.8", {"start": v(-56.15, -48.18) * mm, "mid": v(0, -67.5) * mm, "end": v(56.15, -48.18) * mm});
            skArc(sketch, "E79.9", {"start": v(56.15, -48.18) * mm, "mid": v(58.99, -44.68) * mm, "end": v(60, -40.3) * mm});
            skLineSegment(sketch, "E79.10", {"start": v(60, 40.3) * mm, "end": v(60, -40.3) * mm});
            skArc(sketch, "E79.11", {"start": v(60, 40.3) * mm, "mid": v(58.99, 44.68) * mm, "end": v(56.15, 48.18) * mm});
            skLineSegment(sketch, "E79.12", {"start": v(80, -80) * mm, "end": v(80, 80) * mm});
            skArc(sketch, "E79.13", {"start": v(80, 80) * mm, "mid": v(77.07, 87.07) * mm, "end": v(70, 90) * mm});
            skCircle(sketch, "E79.14", {"center": v(60, 67.5) * mm, "radius": 4 * mm});
            skCircle(sketch, "E79.15", {"center": v(60, -67.5) * mm, "radius": 4 * mm});
            skCircle(sketch, "E79.16", {"center": v(-60, -67.5) * mm, "radius": 4 * mm});
            skArc(sketch, "E79.17", {"start": v(-80, -80) * mm, "mid": v(-77.07, -87.07) * mm, "end": v(-70, -90) * mm});
            skLineSegment(sketch, "E79.18", {"start": v(-70, -90) * mm, "end": v(70, -90) * mm});
            skArc(sketch, "E79.19", {"start": v(70, -90) * mm, "mid": v(77.07, -87.07) * mm, "end": v(80, -80) * mm});
            skLineSegment(sketch, "E80", {"start": v(-33, 90) * mm, "end": v(-15, 108) * mm});
            skLineSegment(sketch, "E81", {"start": v(0, 120) * mm, "end": v(0, 90) * mm, "construction": true});
            skLineSegment(sketch, "E82", {"start": v(-15, 108) * mm, "end": v(-15, 120) * mm});
            skCircle(sketch, "E83", {"center": v(0, 120) * mm, "radius": 6 * mm});
            skArc(sketch, "E84", {"start": v(-15, 120) * mm, "mid": v(0, 135) * mm, "end": v(15, 120) * mm});
            skLineSegment(sketch, "E85", {"start": v(15, 120) * mm, "end": v(15, 108) * mm});
            skLineSegment(sketch, "E86", {"start": v(15, 108) * mm, "end": v(33, 90) * mm});
            skLineSegment(sketch, "E87", {"start": v(-80, 0) * mm, "end": v(80, 0) * mm, "construction": true});
            skLineSegment(sketch, "E88.MirrorCS", {"start": v(-15, -108) * mm, "end": v(-15, -120) * mm});
            skArc(sketch, "E89.MirrorCS", {"start": v(-15, -120) * mm, "mid": v(0, -135) * mm, "end": v(15, -120) * mm});
            skLineSegment(sketch, "E90.MirrorCS", {"start": v(15, -120) * mm, "end": v(15, -108) * mm});
            skCircle(sketch, "E91.MirrorC", {"center": v(0, -120) * mm, "radius": 6 * mm});
            skLineSegment(sketch, "E92.MirrorCS", {"start": v(-33, -90) * mm, "end": v(-15, -108) * mm});
            skLineSegment(sketch, "E93.MirrorCS", {"start": v(15, -108) * mm, "end": v(33, -90) * mm});
            skSolve(sketch);
        }
        {
            var Q0;
            Q0 = qSketchRegion(id + "F16", true);
            var Q1;
            {var subQ0=sQuery(id+"F4.wireOp",EDGE,"E36.filletArc");var subQ1=sQuery(id+"F4.wireOp",EDGE,"E35.filletArc");var subQ2=sQuery(id+"F4.wireOp",EDGE,"E34.filletArc");var subQ3=sQuery(id+"F4.wireOp",EDGE,"E33.filletArc");var subQ4=sQuery(id+"F4.wireOp",EDGE,"E27.0");var subQ5=sQuery(id+"F4.wireOp",EDGE,"E30");var subQ6=sQuery(id+"F4.wireOp",EDGE,"E28.0");var subQ7=sQuery(id+"F4.wireOp",EDGE,"E29");Q1=makeQuery(id+"F6.boolean.opBoolean","SPLIT",FACE,{"disambiguationData":[TD([makeQuery(id+"F5.opExtrude","SWEPT_FACE",FACE,{"disambiguationData":[OSD([subQ4])]})])],"derivedFrom":makeQuery(id+"F5.opExtrude","CAP_FACE",FACE,{"disambiguationData":[OSD([subQ4,subQ6,subQ7,subQ5,subQ3,subQ2,subQ1,subQ0,sQuery(id+"F4.wireOp",EDGE,"E41"),sQuery(id+"F4.wireOp",EDGE,"E42"),sQuery(id+"F4.wireOp",EDGE,"E43"),sQuery(id+"F4.wireOp",EDGE,"E45"),sQuery(id+"F4.wireOp",EDGE,"E46"),sQuery(id+"F4.wireOp",EDGE,"E47.filletArc"),sQuery(id+"F4.wireOp",EDGE,"E48.filletArc"),sQuery(id+"F4.wireOp",EDGE,"E49.filletArc"),sQuery(id+"F4.wireOp",EDGE,"E50.filletArc"),sQuery(id+"F4.wireOp",EDGE,"E51.filletArc"),sQuery(id+"F4.wireOp",EDGE,"E52.filletArc"),sQuery(id+"F4.wireOp",EDGE,"E53.0.MirrorCS"),sQuery(id+"F4.wireOp",EDGE,"E54.0.MirrorCS"),sQuery(id+"F4.wireOp",EDGE,"E55.0.MirrorCS"),sQuery(id+"F4.wireOp",EDGE,"E56.0.MirrorCS"),sQuery(id+"F4.wireOp",EDGE,"E57.0.MirrorCS"),sQuery(id+"F4.wireOp",EDGE,"E58.0.MirrorCS"),sQuery(id+"F4.wireOp",EDGE,"E59.0.MirrorCS"),sQuery(id+"F4.wireOp",EDGE,"E60.0.MirrorCS"),sQuery(id+"F4.wireOp",EDGE,"E61.0.MirrorCS"),sQuery(id+"F4.wireOp",EDGE,"E62.0.MirrorCS"),sQuery(id+"F4.wireOp",EDGE,"E63.0.MirrorCS")])],"isStart":true})});}
            extrude(context, id + "F17", {"entities" : qUnion([Q0]), "endBound" : BoundingType.UP_TO_SURFACE, "endBoundEntityFace" : qUnion([Q1]), "depth" : 25 * mm});
        }
    });
